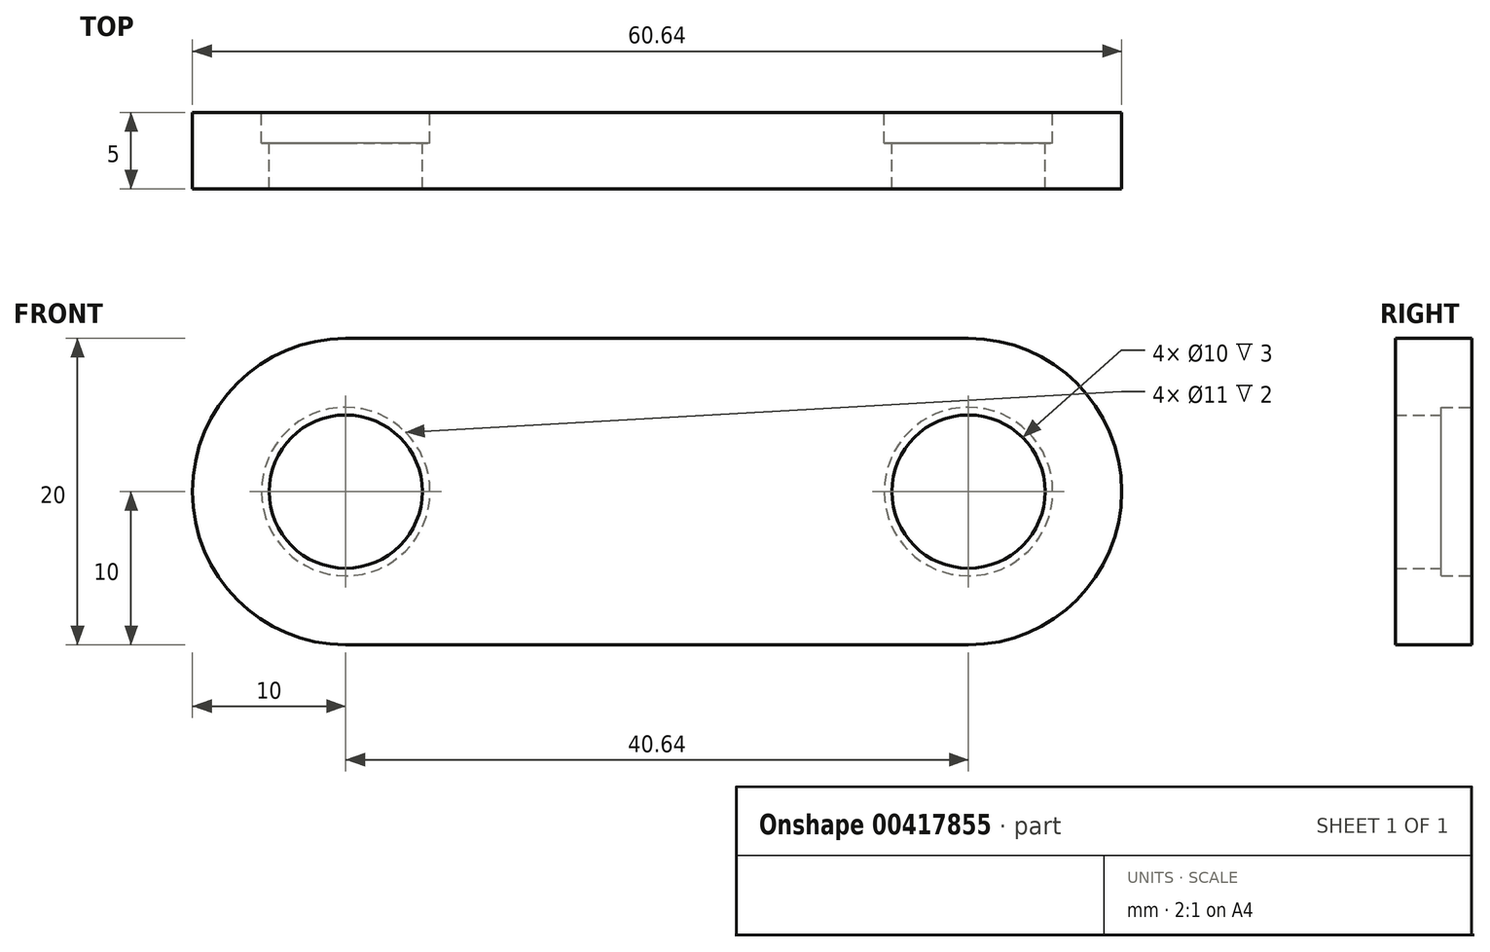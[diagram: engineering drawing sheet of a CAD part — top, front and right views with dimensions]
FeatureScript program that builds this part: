
annotation { "Feature Type Name" : "Feature", "Feature Type Description" : "" }
export const myFeature = defineFeature(function(context is Context, id is Id, definition is map)
    precondition{}
    {
        {
            var Q0;
            Q0=qCreatedBy(makeId("Front.planeOp"),FACE);
            var sketch = newSketch(context, id + "F0", { "sketchPlane" : qUnion([Q0])});
            skArc(sketch, "E0", {"start": v(0, 10) * mm, "mid": v(-10, 0) * mm, "end": v(0, -10) * mm});
            skArc(sketch, "E1", {"start": v(40.64, -10) * mm, "mid": v(50.64, 0) * mm, "end": v(40.64, 10) * mm});
            skCircle(sketch, "E2", {"center": v(0, 0) * mm, "radius": 5 * mm});
            skCircle(sketch, "E3", {"center": v(40.64, 0) * mm, "radius": 5 * mm});
            skLineSegment(sketch, "E4", {"start": v(0, 10) * mm, "end": v(40.64, 10) * mm});
            skLineSegment(sketch, "E5", {"start": v(0, -10) * mm, "end": v(40.64, -10) * mm});
            skCircle(sketch, "E6", {"center": v(40.64, 0) * mm, "radius": 5.5 * mm});
            skCircle(sketch, "E7", {"center": v(0, 0) * mm, "radius": 5.5 * mm});
            skSolve(sketch);
        }
        {
            var Q0;
            Q0=makeQuery(id+"F0.imprint","IMPRINT",FACE,{"disambiguationData":[TD([[makeQuery(id+"F0.imprint","IMPRINT",EDGE,{"derivedFrom":sQuery(id+"F0.wireOp",EDGE,"E0")}),1.0]])]});
            var Q1;
            Q1=makeQuery(id+"F0.imprint","IMPRINT",FACE,{"disambiguationData":[TD([[makeQuery(id+"F0.imprint","IMPRINT",EDGE,{"derivedFrom":sQuery(id+"F0.wireOp",EDGE,"E2")}),-1.0]])]});
            var Q2;
            Q2=makeQuery(id+"F0.imprint","IMPRINT",FACE,{"disambiguationData":[TD([[makeQuery(id+"F0.imprint","IMPRINT",EDGE,{"derivedFrom":sQuery(id+"F0.wireOp",EDGE,"E3")}),-1.0]])]});
            extrude(context, id + "F1", {"entities" : qUnion([Q0, Q1, Q2]), "depth" : 5 * mm});
        }
        {
            var Q0;
            Q0=makeQuery(id+"F0.imprint","IMPRINT",FACE,{"disambiguationData":[TD([[makeQuery(id+"F0.imprint","IMPRINT",EDGE,{"derivedFrom":sQuery(id+"F0.wireOp",EDGE,"E3")}),-1.0]])]});
            var Q1;
            Q1=makeQuery(id+"F0.imprint","IMPRINT",FACE,{"disambiguationData":[TD([[makeQuery(id+"F0.imprint","IMPRINT",EDGE,{"derivedFrom":sQuery(id+"F0.wireOp",EDGE,"E2")}),-1.0]])]});
            extrude(context, id + "F2", {"entities" : qUnion([Q0, Q1]), "operationType" : NewBodyOperationType.REMOVE, "depth" : 2 * mm});
        }
    });
